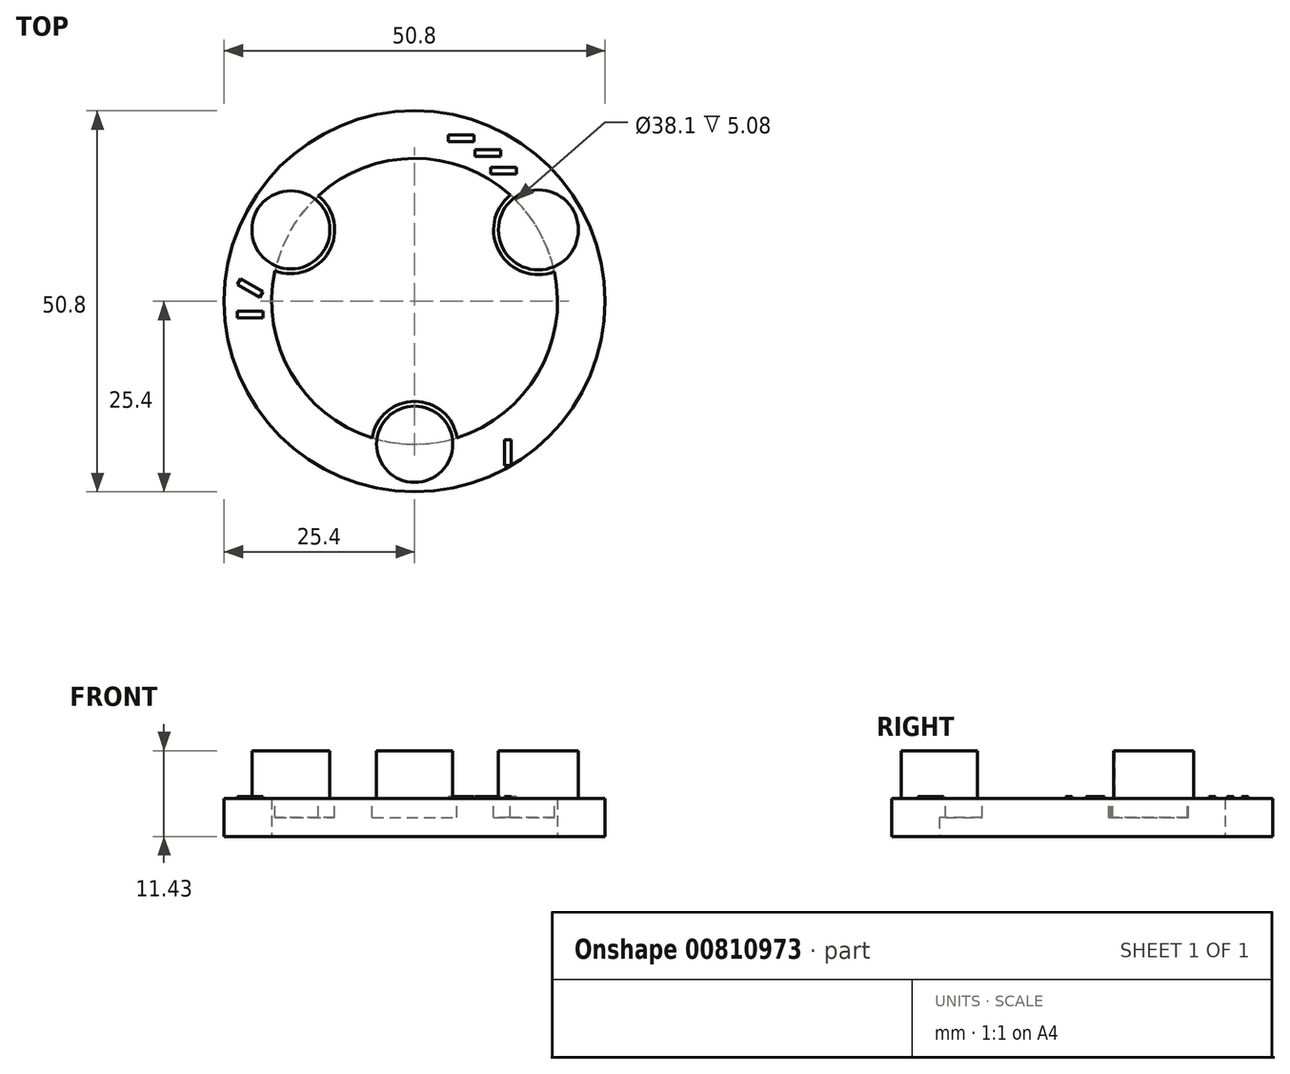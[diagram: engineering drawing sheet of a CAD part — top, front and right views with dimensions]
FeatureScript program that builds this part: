
annotation { "Feature Type Name" : "Feature", "Feature Type Description" : "" }
export const myFeature = defineFeature(function(context is Context, id is Id, definition is map)
    precondition{}
    {
        {
            var Q0;
            Q0=qCreatedBy(makeId("Top.planeOp"),FACE);
            var sketch = newSketch(context, id + "F0", { "sketchPlane" : qUnion([Q0])});
            skCircle(sketch, "E0", {"center": v(0, 0) * mm, "radius": 25.4 * mm});
            skCircle(sketch, "E1", {"center": v(0, 0) * mm, "radius": 19.05 * mm});
            skSolve(sketch);
        }
        {
            var Q0;
            Q0=makeQuery(id+"F0.imprint","IMPRINT",FACE,{"disambiguationData":[TD([[makeQuery(id+"F0.imprint","IMPRINT",EDGE,{"derivedFrom":sQuery(id+"F0.wireOp",EDGE,"E0")}),1.0]])]});
            extrude(context, id + "F1", {"entities" : qUnion([Q0]), "endBound" : BoundingType.SYMMETRIC, "depth" : 5.08 * mm, "offsetDistance" : 25.4 * mm});
        }
        {
            var Q0;
            Q0=makeQuery(id+"F1.opExtrude","CAP_FACE",FACE,{"disambiguationData":[OSD([sQuery(id+"F0.wireOp",EDGE,"E0"),sQuery(id+"F0.wireOp",EDGE,"E1")])],"isStart":false});
            var sketch = newSketch(context, id + "F2", { "sketchPlane" : qUnion([Q0])});
            skCircle(sketch, "E2", {"center": v(0, -19.05) * mm, "radius": 5.72 * mm});
            skCircle(sketch, "E3", {"center": v(0, -19.05) * mm, "radius": 5.08 * mm});
            skCircle(sketch, "E4.1.0", {"center": v(16.5, 9.52) * mm, "radius": 5.33 * mm});
            skCircle(sketch, "E4.1.1", {"center": v(16.5, 9.52) * mm, "radius": 5.97 * mm});
            skCircle(sketch, "E4.2.0", {"center": v(-16.5, 9.53) * mm, "radius": 5.2 * mm});
            skCircle(sketch, "E4.2.1", {"center": v(-16.5, 9.53) * mm, "radius": 5.84 * mm});
            skPoint(sketch, "E4.center", {"position": v(0, 0) * mm});
            skSolve(sketch);
        }
        {
            var Q0;
            Q0 = qSketchRegion(id + "F2", true);
            var Q1;
            {var subQ0=sQuery(id+"F2.wireOp",EDGE,"E4.2.0");var subQ1=makeQuery(id+"F1.opExtrude","CAP_EDGE",EDGE,{"disambiguationData":[OSD([sQuery(id+"F0.wireOp",EDGE,"E1")])],"isStart":false});var subQ2=makeQuery(id+"F2.imprint","INTERSECT",VERTEX,{"disambiguationData":[OD(0.0)],"derivedFrom":[subQ1,subQ0]});Q1=makeQuery(id+"F2.imprint","IMPRINT",FACE,{"disambiguationData":[TD([[makeQuery(id+"F2.imprint","IMPRINT",EDGE,{"disambiguationData":[TD([[subQ2,1.0]])],"derivedFrom":subQ0}),1.0]])]});}
            var Q2;
            {var subQ0=sQuery(id+"F2.wireOp",EDGE,"E4.2.0");var subQ1=makeQuery(id+"F1.opExtrude","CAP_EDGE",EDGE,{"disambiguationData":[OSD([sQuery(id+"F0.wireOp",EDGE,"E1")])],"isStart":false});var subQ2=makeQuery(id+"F2.imprint","INTERSECT",VERTEX,{"disambiguationData":[OD(0.0)],"derivedFrom":[subQ1,subQ0]});Q2=makeQuery(id+"F2.imprint","IMPRINT",FACE,{"disambiguationData":[TD([[makeQuery(id+"F2.imprint","IMPRINT",EDGE,{"disambiguationData":[TD([[subQ2,-1.0]])],"derivedFrom":subQ0}),1.0]])]});}
            var Q3;
            {var subQ0=sQuery(id+"F2.wireOp",EDGE,"E4.1.0");var subQ1=makeQuery(id+"F1.opExtrude","CAP_EDGE",EDGE,{"disambiguationData":[OSD([sQuery(id+"F0.wireOp",EDGE,"E1")])],"isStart":false});var subQ2=makeQuery(id+"F2.imprint","INTERSECT",VERTEX,{"disambiguationData":[OD(0.0)],"derivedFrom":[subQ1,subQ0]});Q3=makeQuery(id+"F2.imprint","IMPRINT",FACE,{"disambiguationData":[TD([[makeQuery(id+"F2.imprint","IMPRINT",EDGE,{"disambiguationData":[TD([[subQ2,1.0]])],"derivedFrom":subQ0}),1.0]])]});}
            var Q4;
            {var subQ0=sQuery(id+"F2.wireOp",EDGE,"E4.1.0");var subQ1=makeQuery(id+"F1.opExtrude","CAP_EDGE",EDGE,{"disambiguationData":[OSD([sQuery(id+"F0.wireOp",EDGE,"E1")])],"isStart":false});var subQ2=makeQuery(id+"F2.imprint","INTERSECT",VERTEX,{"disambiguationData":[OD(0.0)],"derivedFrom":[subQ1,subQ0]});Q4=makeQuery(id+"F2.imprint","IMPRINT",FACE,{"disambiguationData":[TD([[makeQuery(id+"F2.imprint","IMPRINT",EDGE,{"disambiguationData":[TD([[subQ2,-1.0]])],"derivedFrom":subQ0}),1.0]])]});}
            var Q5;
            {var subQ0=sQuery(id+"F2.wireOp",EDGE,"E3");var subQ1=makeQuery(id+"F1.opExtrude","CAP_EDGE",EDGE,{"disambiguationData":[OSD([sQuery(id+"F0.wireOp",EDGE,"E1")])],"isStart":false});var subQ2=makeQuery(id+"F2.imprint","INTERSECT",VERTEX,{"disambiguationData":[OD(0.0)],"derivedFrom":[subQ1,subQ0]});Q5=makeQuery(id+"F2.imprint","IMPRINT",FACE,{"disambiguationData":[TD([[makeQuery(id+"F2.imprint","IMPRINT",EDGE,{"disambiguationData":[TD([[subQ2,1.0]])],"derivedFrom":subQ0}),1.0]])]});}
            var Q6;
            {var subQ0=sQuery(id+"F2.wireOp",EDGE,"E3");var subQ1=makeQuery(id+"F1.opExtrude","CAP_EDGE",EDGE,{"disambiguationData":[OSD([sQuery(id+"F0.wireOp",EDGE,"E1")])],"isStart":false});var subQ2=makeQuery(id+"F2.imprint","INTERSECT",VERTEX,{"disambiguationData":[OD(0.0)],"derivedFrom":[subQ1,subQ0]});Q6=makeQuery(id+"F2.imprint","IMPRINT",FACE,{"disambiguationData":[TD([[makeQuery(id+"F2.imprint","IMPRINT",EDGE,{"disambiguationData":[TD([[subQ2,-1.0]])],"derivedFrom":subQ0}),1.0]])]});}
            extrude(context, id + "F3", {"entities" : qUnion([Q0, Q1, Q2, Q3, Q4, Q5, Q6]), "operationType" : NewBodyOperationType.ADD, "oppositeDirection" : true, "depth" : 2.54 * mm, "offsetDistance" : 25.4 * mm});
        }
        {
            var Q0;
            {var subQ0=sQuery(id+"F2.wireOp",EDGE,"E4.2.0");var subQ1=makeQuery(id+"F1.opExtrude","CAP_EDGE",EDGE,{"disambiguationData":[OSD([sQuery(id+"F0.wireOp",EDGE,"E1")])],"isStart":false});var subQ2=makeQuery(id+"F2.imprint","INTERSECT",VERTEX,{"disambiguationData":[OD(0.0)],"derivedFrom":[subQ1,subQ0]});Q0=makeQuery(id+"F2.imprint","IMPRINT",FACE,{"disambiguationData":[TD([[makeQuery(id+"F2.imprint","IMPRINT",EDGE,{"disambiguationData":[TD([[subQ2,1.0]])],"derivedFrom":subQ0}),1.0]])]});}
            var Q1;
            {var subQ0=sQuery(id+"F2.wireOp",EDGE,"E4.2.0");var subQ1=makeQuery(id+"F1.opExtrude","CAP_EDGE",EDGE,{"disambiguationData":[OSD([sQuery(id+"F0.wireOp",EDGE,"E1")])],"isStart":false});var subQ2=makeQuery(id+"F2.imprint","INTERSECT",VERTEX,{"disambiguationData":[OD(0.0)],"derivedFrom":[subQ1,subQ0]});Q1=makeQuery(id+"F2.imprint","IMPRINT",FACE,{"disambiguationData":[TD([[makeQuery(id+"F2.imprint","IMPRINT",EDGE,{"disambiguationData":[TD([[subQ2,-1.0]])],"derivedFrom":subQ0}),1.0]])]});}
            var Q2;
            {var subQ0=sQuery(id+"F2.wireOp",EDGE,"E4.1.0");var subQ1=makeQuery(id+"F1.opExtrude","CAP_EDGE",EDGE,{"disambiguationData":[OSD([sQuery(id+"F0.wireOp",EDGE,"E1")])],"isStart":false});var subQ2=makeQuery(id+"F2.imprint","INTERSECT",VERTEX,{"disambiguationData":[OD(0.0)],"derivedFrom":[subQ1,subQ0]});Q2=makeQuery(id+"F2.imprint","IMPRINT",FACE,{"disambiguationData":[TD([[makeQuery(id+"F2.imprint","IMPRINT",EDGE,{"disambiguationData":[TD([[subQ2,1.0]])],"derivedFrom":subQ0}),1.0]])]});}
            var Q3;
            {var subQ0=sQuery(id+"F2.wireOp",EDGE,"E4.1.0");var subQ1=makeQuery(id+"F1.opExtrude","CAP_EDGE",EDGE,{"disambiguationData":[OSD([sQuery(id+"F0.wireOp",EDGE,"E1")])],"isStart":false});var subQ2=makeQuery(id+"F2.imprint","INTERSECT",VERTEX,{"disambiguationData":[OD(0.0)],"derivedFrom":[subQ1,subQ0]});Q3=makeQuery(id+"F2.imprint","IMPRINT",FACE,{"disambiguationData":[TD([[makeQuery(id+"F2.imprint","IMPRINT",EDGE,{"disambiguationData":[TD([[subQ2,-1.0]])],"derivedFrom":subQ0}),1.0]])]});}
            var Q4;
            {var subQ0=sQuery(id+"F2.wireOp",EDGE,"E3");var subQ1=makeQuery(id+"F1.opExtrude","CAP_EDGE",EDGE,{"disambiguationData":[OSD([sQuery(id+"F0.wireOp",EDGE,"E1")])],"isStart":false});var subQ2=makeQuery(id+"F2.imprint","INTERSECT",VERTEX,{"disambiguationData":[OD(0.0)],"derivedFrom":[subQ1,subQ0]});Q4=makeQuery(id+"F2.imprint","IMPRINT",FACE,{"disambiguationData":[TD([[makeQuery(id+"F2.imprint","IMPRINT",EDGE,{"disambiguationData":[TD([[subQ2,1.0]])],"derivedFrom":subQ0}),1.0]])]});}
            var Q5;
            {var subQ0=sQuery(id+"F2.wireOp",EDGE,"E3");var subQ1=makeQuery(id+"F1.opExtrude","CAP_EDGE",EDGE,{"disambiguationData":[OSD([sQuery(id+"F0.wireOp",EDGE,"E1")])],"isStart":false});var subQ2=makeQuery(id+"F2.imprint","INTERSECT",VERTEX,{"disambiguationData":[OD(0.0)],"derivedFrom":[subQ1,subQ0]});Q5=makeQuery(id+"F2.imprint","IMPRINT",FACE,{"disambiguationData":[TD([[makeQuery(id+"F2.imprint","IMPRINT",EDGE,{"disambiguationData":[TD([[subQ2,-1.0]])],"derivedFrom":subQ0}),1.0]])]});}
            extrude(context, id + "F4", {"entities" : qUnion([Q0, Q1, Q2, Q3, Q4, Q5]), "operationType" : NewBodyOperationType.ADD, "depth" : 6.35 * mm, "offsetDistance" : 25.4 * mm});
        }
        {
            var Q0;
            Q0=makeQuery(id+"F2.imprint","IMPRINT",FACE,{"disambiguationData":[TD([[makeQuery(id+"F2.imprint","IMPRINT",EDGE,{"derivedFrom":makeQuery(id+"F1.opExtrude","CAP_EDGE",EDGE,{"disambiguationData":[OSD([sQuery(id+"F0.wireOp",EDGE,"E0")])],"isStart":false})}),1.0]])]});
            var sketch = newSketch(context, id + "F5", { "sketchPlane" : qUnion([Q0])});
            skCircle(sketch, "E5.0.0", {"center": v(0, 0) * mm, "radius": 25.4 * mm});
            skLineSegment(sketch, "E6.bottom", {"start": v(12.88, -21.9) * mm, "end": v(12, -21.9) * mm});
            skLineSegment(sketch, "E6.top", {"start": v(12.88, -18.46) * mm, "end": v(12, -18.46) * mm});
            skLineSegment(sketch, "E6.left", {"start": v(12.88, -21.9) * mm, "end": v(12.88, -18.46) * mm});
            skLineSegment(sketch, "E6.right", {"start": v(12, -21.9) * mm, "end": v(12, -18.46) * mm});
            skLineSegment(sketch, "E7.2.0", {"start": v(-23.64, 2.23) * mm, "end": v(-20.67, 0.52) * mm});
            skLineSegment(sketch, "E7.2.1", {"start": v(-23.2, 3) * mm, "end": v(-20.22, 1.29) * mm});
            skLineSegment(sketch, "E7.2.2", {"start": v(-20.67, 0.52) * mm, "end": v(-20.22, 1.29) * mm});
            skLineSegment(sketch, "E7.2.3", {"start": v(-23.64, 2.23) * mm, "end": v(-23.2, 3) * mm});
            skPoint(sketch, "E7.center", {"position": v(1.59, 0.71) * mm});
            skLineSegment(sketch, "E8.bottom", {"start": v(-23.67, -2.18) * mm, "end": v(-20.24, -2.18) * mm});
            skLineSegment(sketch, "E8.top", {"start": v(-23.67, -1.3) * mm, "end": v(-20.24, -1.3) * mm});
            skLineSegment(sketch, "E8.left", {"start": v(-23.67, -2.18) * mm, "end": v(-23.67, -1.3) * mm});
            skLineSegment(sketch, "E8.right", {"start": v(-20.24, -2.18) * mm, "end": v(-20.24, -1.3) * mm});
            skPoint(sketch, "E8.middle", {"position": v(-21.96, -1.74) * mm});
            skLineSegment(sketch, "E9.bottom", {"start": v(13.55, 16.95) * mm, "end": v(10.12, 16.95) * mm});
            skLineSegment(sketch, "E9.top", {"start": v(13.55, 17.84) * mm, "end": v(10.12, 17.84) * mm});
            skLineSegment(sketch, "E9.left", {"start": v(13.55, 16.95) * mm, "end": v(13.55, 17.84) * mm});
            skLineSegment(sketch, "E9.right", {"start": v(10.12, 16.95) * mm, "end": v(10.12, 17.84) * mm});
            skPoint(sketch, "E9.middle", {"position": v(11.84, 17.4) * mm});
            skLineSegment(sketch, "E10.bottom", {"start": v(11.45, 19.3) * mm, "end": v(8.03, 19.3) * mm});
            skLineSegment(sketch, "E10.top", {"start": v(11.45, 20.2) * mm, "end": v(8.03, 20.2) * mm});
            skLineSegment(sketch, "E10.left", {"start": v(11.45, 19.3) * mm, "end": v(11.45, 20.2) * mm});
            skLineSegment(sketch, "E10.right", {"start": v(8.03, 19.3) * mm, "end": v(8.03, 20.2) * mm});
            skPoint(sketch, "E10.middle", {"position": v(9.74, 19.75) * mm});
            skLineSegment(sketch, "E11.bottom", {"start": v(7.93, 21.29) * mm, "end": v(4.5, 21.29) * mm});
            skLineSegment(sketch, "E11.top", {"start": v(7.93, 22.18) * mm, "end": v(4.5, 22.18) * mm});
            skLineSegment(sketch, "E11.left", {"start": v(7.93, 21.29) * mm, "end": v(7.93, 22.18) * mm});
            skLineSegment(sketch, "E11.right", {"start": v(4.5, 21.29) * mm, "end": v(4.5, 22.18) * mm});
            skPoint(sketch, "E11.middle", {"position": v(6.21, 21.73) * mm});
            skSolve(sketch);
        }
        {
            var Q0;
            Q0=makeQuery(id+"F5.imprint","IMPRINT",FACE,{"disambiguationData":[TD([[makeQuery(id+"F5.imprint","IMPRINT",EDGE,{"derivedFrom":sQuery(id+"F5.wireOp",EDGE,"E10.bottom")}),-1.0]])]});
            var Q1;
            Q1=makeQuery(id+"F5.imprint","IMPRINT",FACE,{"disambiguationData":[TD([[makeQuery(id+"F5.imprint","IMPRINT",EDGE,{"derivedFrom":sQuery(id+"F5.wireOp",EDGE,"E9.bottom")}),-1.0]])]});
            var Q2;
            Q2=makeQuery(id+"F5.imprint","IMPRINT",FACE,{"disambiguationData":[TD([[makeQuery(id+"F5.imprint","IMPRINT",EDGE,{"derivedFrom":sQuery(id+"F5.wireOp",EDGE,"E11.bottom")}),-1.0]])]});
            var Q3;
            Q3=makeQuery(id+"F5.imprint","IMPRINT",FACE,{"disambiguationData":[TD([[makeQuery(id+"F5.imprint","IMPRINT",EDGE,{"derivedFrom":sQuery(id+"F5.wireOp",EDGE,"E8.bottom")}),1.0]])]});
            var Q4;
            Q4=makeQuery(id+"F5.imprint","IMPRINT",FACE,{"disambiguationData":[TD([[makeQuery(id+"F5.imprint","IMPRINT",EDGE,{"derivedFrom":sQuery(id+"F5.wireOp",EDGE,"E7.2.0")}),1.0]])]});
            var Q5;
            Q5=makeQuery(id+"F5.imprint","IMPRINT",FACE,{"disambiguationData":[TD([[makeQuery(id+"F5.imprint","IMPRINT",EDGE,{"derivedFrom":sQuery(id+"F5.wireOp",EDGE,"E6.bottom")}),-1.0]])]});
            var Q6;
            Q6=makeQuery(id+"F1.opExtrude","SWEPT_BODY",BODY,{"disambiguationData":[OSD([sQuery(id+"F0.wireOp",EDGE,"E0"),sQuery(id+"F0.wireOp",EDGE,"E1")])]});
            extrude(context, id + "F6", {"entities" : qUnion([Q0, Q1, Q2, Q3, Q4, Q5]), "operationType" : NewBodyOperationType.ADD, "depth" : 0.25 * mm, "endBoundEntityBody" : qUnion([Q6]), "offsetDistance" : 25.4 * mm});
        }
    });
